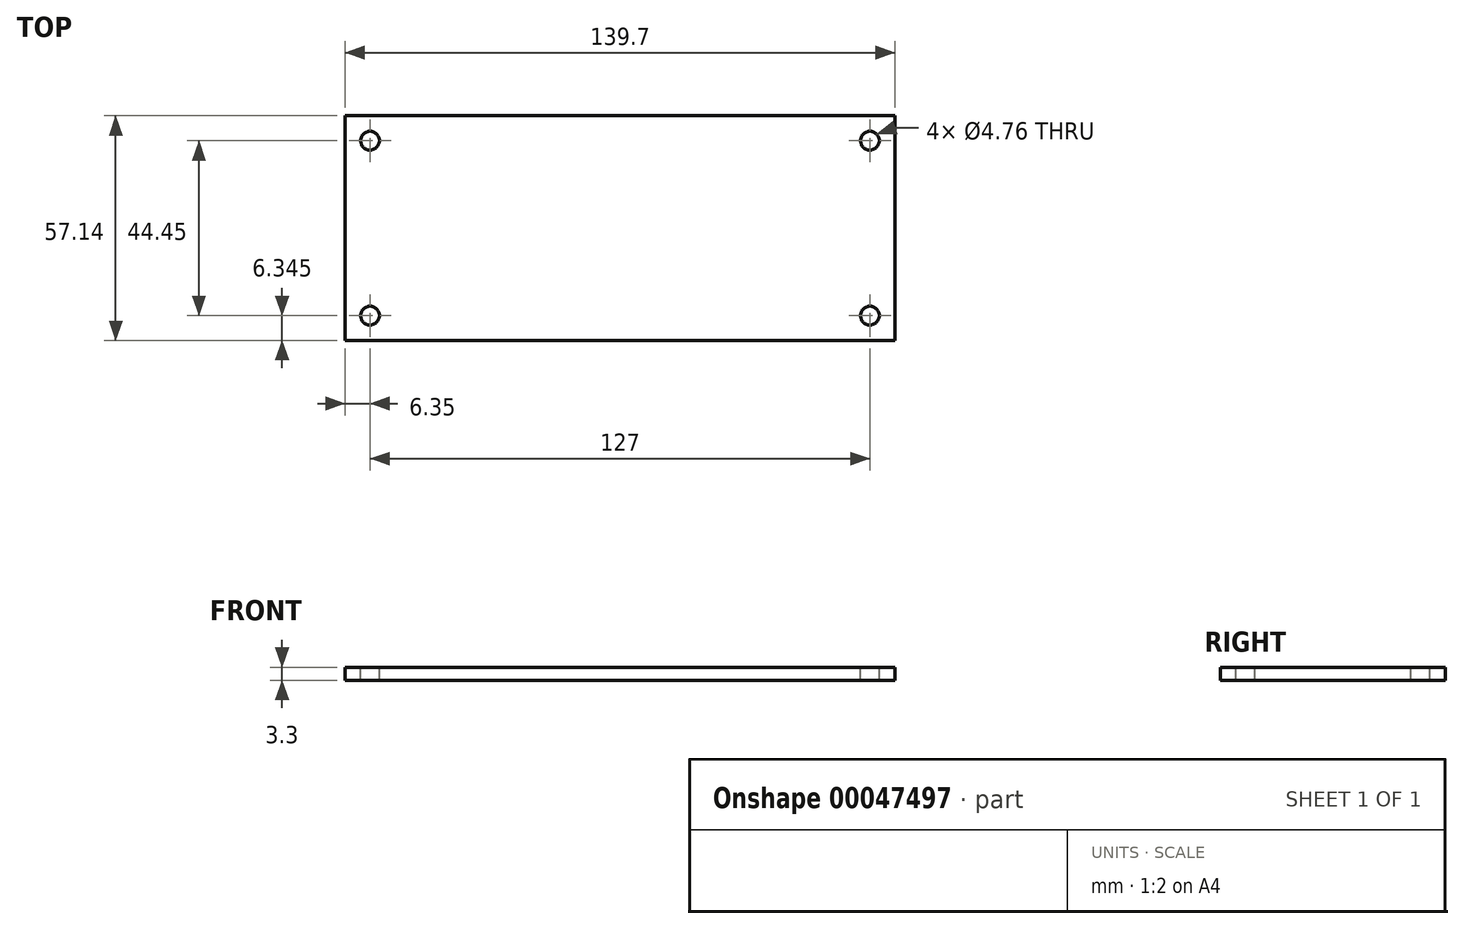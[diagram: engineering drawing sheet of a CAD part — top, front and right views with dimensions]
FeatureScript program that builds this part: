
annotation { "Feature Type Name" : "Feature", "Feature Type Description" : "" }
export const myFeature = defineFeature(function(context is Context, id is Id, definition is map)
    precondition{}
    {
        {
            var Q0;
            Q0=qCreatedBy(makeId("Top.planeOp"),FACE);
            var sketch = newSketch(context, id + "F0", { "sketchPlane" : qUnion([Q0])});
            skLineSegment(sketch, "E0.rect.bottom", {"start": v(69.85, 28.58) * mm, "end": v(-69.85, 28.58) * mm});
            skLineSegment(sketch, "E0.rect.top", {"start": v(69.85, -28.58) * mm, "end": v(-69.85, -28.58) * mm});
            skLineSegment(sketch, "E0.rect.left", {"start": v(69.85, 28.58) * mm, "end": v(69.85, -28.58) * mm});
            skLineSegment(sketch, "E0.rect.right", {"start": v(-69.85, 28.58) * mm, "end": v(-69.85, -28.57) * mm});
            skPoint(sketch, "E0.rect.middle", {"position": v(0, 0) * mm});
            skSolve(sketch);
        }
        {
            var Q0;
            Q0 = qSketchRegion(id + "F0", true);
            extrude(context, id + "F1", {"entities" : qUnion([Q0]), "depth" : 3.3 * mm, "symmetric" : true});
        }
        {
            var Q0;
            Q0=makeQuery(id+"F1.opExtrude","CAP_FACE",FACE,{"disambiguationData":[OSD([sQuery(id+"F0.wireOp",EDGE,"E0.rect.bottom"),sQuery(id+"F0.wireOp",EDGE,"E0.rect.top"),sQuery(id+"F0.wireOp",EDGE,"E0.rect.left"),sQuery(id+"F0.wireOp",EDGE,"E0.rect.right")])],"isStart":false});
            var sketch = newSketch(context, id + "F2", { "sketchPlane" : qUnion([Q0])});
            skCircle(sketch, "E1", {"center": v(-63.5, 22.23) * mm, "radius": 2.38 * mm});
            skCircle(sketch, "E2.MirrorC", {"center": v(63.5, 22.23) * mm, "radius": 2.38 * mm});
            skCircle(sketch, "E3.MirrorC", {"center": v(-63.5, -22.23) * mm, "radius": 2.38 * mm});
            skCircle(sketch, "E4.MirrorC", {"center": v(63.5, -22.23) * mm, "radius": 2.38 * mm});
            skSolve(sketch);
        }
        {
            var Q0;
            Q0 = qSketchRegion(id + "F2", true);
            var Q1;
            Q1=makeQuery(id+"F1.opExtrude","CAP_FACE",FACE,{"disambiguationData":[OSD([sQuery(id+"F0.wireOp",EDGE,"E0.rect.bottom"),sQuery(id+"F0.wireOp",EDGE,"E0.rect.top"),sQuery(id+"F0.wireOp",EDGE,"E0.rect.left"),sQuery(id+"F0.wireOp",EDGE,"E0.rect.right")])],"isStart":true});
            extrude(context, id + "F3", {"entities" : qUnion([Q0]), "operationType" : NewBodyOperationType.REMOVE, "endBound" : BoundingType.UP_TO_SURFACE, "oppositeDirection" : true, "endBoundEntityFace" : qUnion([Q1]), "depth" : 25.4 * mm});
        }
    });
